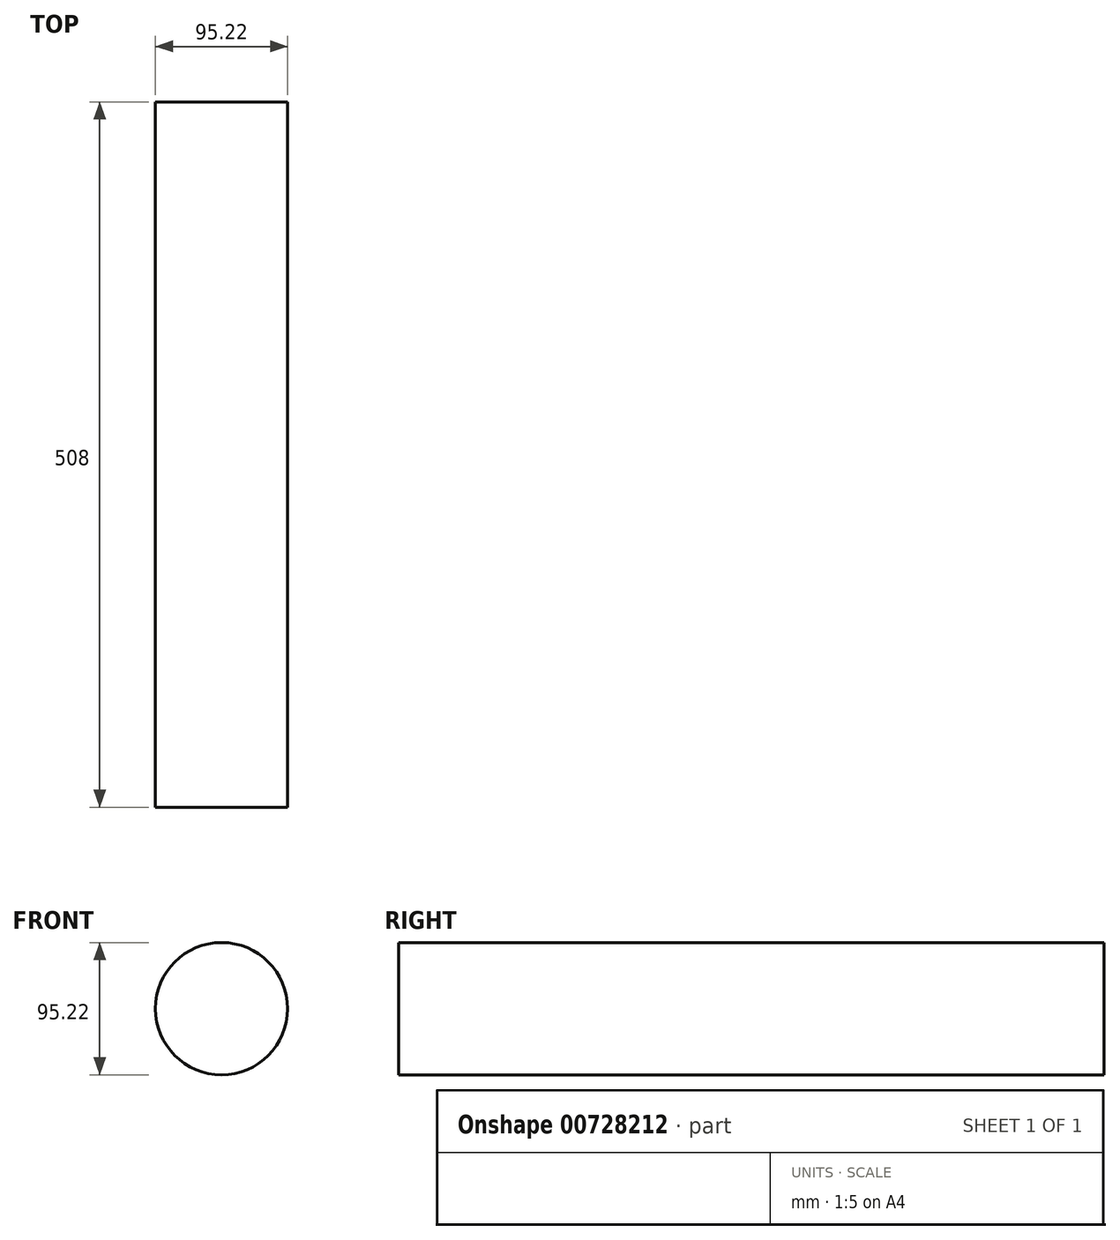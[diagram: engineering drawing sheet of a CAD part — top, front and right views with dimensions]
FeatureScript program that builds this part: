
annotation { "Feature Type Name" : "Feature", "Feature Type Description" : "" }
export const myFeature = defineFeature(function(context is Context, id is Id, definition is map)
    precondition{}
    {
        {
            var Q0;
            Q0=qCreatedBy(makeId("Front.planeOp"),FACE);
            var sketch = newSketch(context, id + "F0", { "sketchPlane" : qUnion([Q0])});
            skCircle(sketch, "E0", {"center": v(0, 0) * mm, "radius": 47.61 * mm});
            skSolve(sketch);
        }
        {
            var Q0;
            Q0 = qSketchRegion(id + "F0", true);
            extrude(context, id + "F1", {"entities" : qUnion([Q0]), "depth" : 254 * mm, "offsetDistance" : 25.4 * mm, "hasSecondDirection" : true, "secondDirectionOppositeDirection" : true, "secondDirectionDepth" : 254 * mm});
        }
        {
            var Q0;
            Q0=qCreatedBy(makeId("Top.planeOp"),FACE);
            var sketch = newSketch(context, id + "F2", { "sketchPlane" : qUnion([Q0])});
            skLineSegment(sketch, "E1", {"start": v(-260.54, -28.97) * mm, "end": v(-27.72, -262.76) * mm});
            skFitSpline(sketch, "E2", {"points": [v(-255.87, 14.88) * mm, v(-54.67, 239.21) * mm, v(254.02, 51.97) * mm], "startDerivative": vector(381.01, 667.6) * mm, "endDerivative": vector(634.95, -574.7) * mm});
            skSolve(sketch);
        }
        {
            var Q0;
            Q0=sQuery(id+"F2.wireOp",EDGE,"E1");
            extrude(context, id + "F3", {"bodyType" : ToolBodyType.SURFACE, "surfaceEntities" : qUnion([Q0]), "depth" : 25.4 * mm, "offsetDistance" : 25.4 * mm, "hasSecondDirection" : true, "secondDirectionOppositeDirection" : true, "secondDirectionDepth" : 25.4 * mm});
        }
    });
